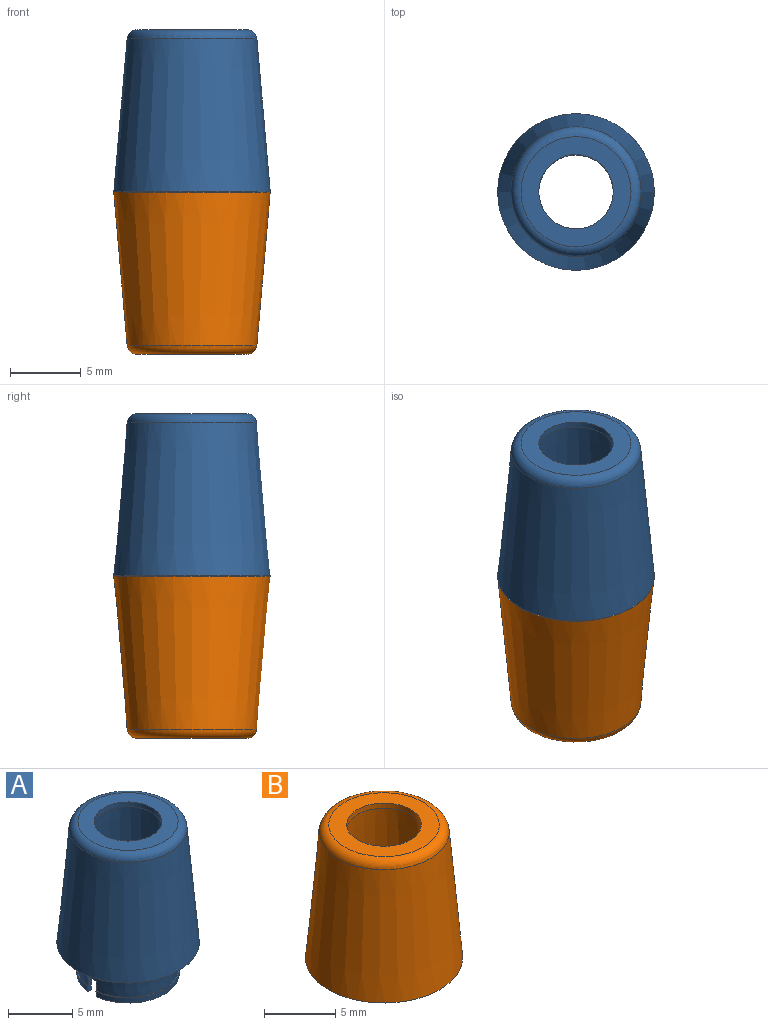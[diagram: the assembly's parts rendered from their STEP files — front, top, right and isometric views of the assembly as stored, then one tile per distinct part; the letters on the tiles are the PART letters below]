
ASSEMBLY  parts=2 mates=1
PART A: 22 faces, bbox 11.1x11.1x14.4 mm
  f0: cone r=3.43mm half-angle=4deg, axis (0,0,-1), area 63.9mm2, adj f1,f12,f14,f16,f17,f18,f19,f20
  f1: plane 7.88x3.51mm, normal (0,0,-1), area 3.6mm2, adj f0,f2,f18,f19
  f2: cone r=4.17mm half-angle=4deg, axis (0,0,1), area 5.8mm2, adj f1,f3,f18,f19
  f3: plane 7.95x3.54mm, normal (0,0,1), area 1.2mm2, adj f2,f4,f18,f19
  f4: cone r=4.12mm half-angle=5deg, axis (0,0,1), area 61.3mm2, adj f3,f7,f15,f16,f17,f18,f19,f20
  f5: cone r=5.53mm half-angle=5deg, axis (0,0,-1), area 344.2mm2, adj f7,f11
  f6: plane 7.77x7.77mm, normal (0,0,1), area 25.7mm2, adj f10,f11
  f7: plane 11.05x11.05mm, normal (0,0,-1), area 42.7mm2, adj f4,f5
  f8: cone r=4.17mm half-angle=5deg, axis (0,0,-1), area 148.5mm2, adj f9,f14
  f9: plane 6.43x6.43mm, normal (0,0,-1), area 10.8mm2, adj f8,f10
  f10: cylinder r=2.62mm len=5.25mm, axis (0,0,1), area 7.3mm2, adj f6,f9
  f11: torus R=3.88mm, axis (0,0,1), area 28.1mm2, adj f5,f6
  f12: plane 7.88x3.51mm, normal (0,0,-1), area 3.6mm2, adj f0,f13,f17,f20
  f13: cone r=4.17mm half-angle=4deg, axis (0,0,1), area 5.8mm2, adj f12,f15,f17,f20
  f14: cone r=3.43mm half-angle=5deg, axis (0,0,1), area 97.7mm2, adj f0,f8
  f15: plane 7.95x3.54mm, normal (0,0,1), area 1.2mm2, adj f4,f13,f17,f20
  f16: plane 0.92x0.48mm, normal (0,0,-1), area 0.4mm2, adj f0,f4,f17,f18
  f17: plane 1.5x0.47mm, normal (0,1,0), area 0.6mm2, adj f0,f4,f12,f13,f15,f16
  f18: plane 1.5x0.47mm, normal (0,-1,0), area 0.6mm2, adj f0,f1,f2,f3,f4,f16
  f19: plane 1.5x0.47mm, normal (0,-1,0), area 0.6mm2, adj f0,f1,f2,f3,f4,f21
  f20: plane 1.5x0.47mm, normal (0,1,0), area 0.6mm2, adj f0,f4,f12,f13,f15,f21
  f21: plane 0.92x0.48mm, normal (0,0,-1), area 0.4mm2, adj f0,f4,f19,f20
PART B: 8 faces, bbox 11.5x11.5x11.4 mm
  f0: cone r=5.53mm half-angle=5deg, axis (0,0,-1), area 344.2mm2, adj f2,f7
  f1: plane 7.77x7.77mm, normal (0,0,1), area 25.7mm2, adj f5,f7
  f2: plane 11.05x11.05mm, normal (0,0,-1), area 23mm2, adj f0,f6
  f3: cone r=4.17mm half-angle=5deg, axis (0,0,-1), area 239.6mm2, adj f4,f6
  f4: plane 6.43x6.43mm, normal (0,0,-1), area 10.8mm2, adj f3,f5
  f5: cylinder r=2.62mm len=5.25mm, axis (0,0,1), area 7.3mm2, adj f1,f4
  f6: torus R=4.82mm, axis (0,0,1), area 28.6mm2, adj f2,f3
  f7: torus R=3.88mm, axis (0,0,1), area 28.1mm2, adj f0,f1
PLACE A t=(-1.5,2.69,1.1)mm fixed
PLACE B rot(axis=(0,1,0),180deg) t=(-1.5,2.69,1.08)mm
MATE slider B.f3 <-> A.f2  axis (0,0,-1) through (-1.5,2.69,0.44)mm
